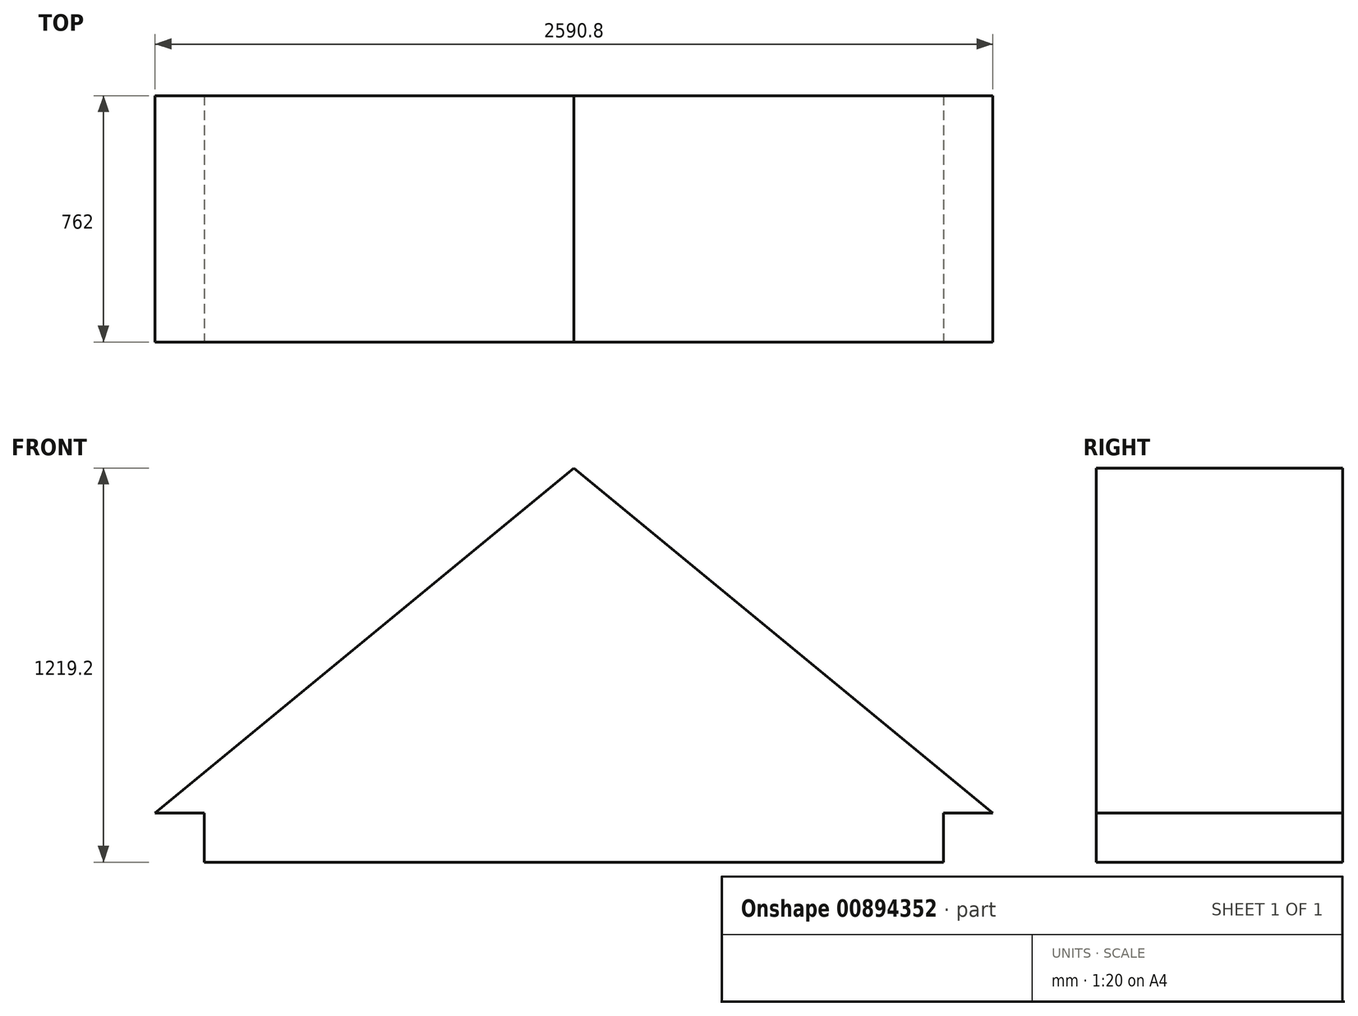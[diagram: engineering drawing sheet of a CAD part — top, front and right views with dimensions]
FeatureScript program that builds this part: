
annotation { "Feature Type Name" : "Feature", "Feature Type Description" : "" }
export const myFeature = defineFeature(function(context is Context, id is Id, definition is map)
    precondition{}
    {
        {
            var Q0;
            Q0=qCreatedBy(makeId("Front.planeOp"),FACE);
            var sketch = newSketch(context, id + "F0", { "sketchPlane" : qUnion([Q0])});
            skLineSegment(sketch, "E0", {"start": v(0, 1057.68) * mm, "end": v(1295.4, -9.12) * mm});
            skLineSegment(sketch, "E1", {"start": v(-1295.4, -9.12) * mm, "end": v(0, 1057.68) * mm});
            skLineSegment(sketch, "E2", {"start": v(1143, -9.12) * mm, "end": v(1143, -161.52) * mm});
            skLineSegment(sketch, "E3", {"start": v(1143, -161.52) * mm, "end": v(-1143, -161.52) * mm});
            skLineSegment(sketch, "E4", {"start": v(-1143, -161.52) * mm, "end": v(-1143, -9.12) * mm});
            skLineSegment(sketch, "E5", {"start": v(1295.4, -9.12) * mm, "end": v(1143, -9.12) * mm});
            skLineSegment(sketch, "E6", {"start": v(-1143, -9.12) * mm, "end": v(-1295.4, -9.12) * mm});
            skSolve(sketch);
        }
        {
            var Q0;
            Q0 = qSketchRegion(id + "F0", true);
            extrude(context, id + "F1", {"entities" : qUnion([Q0]), "oppositeDirection" : true, "depth" : 762 * mm, "offsetDistance" : 25.4 * mm});
        }
    });
